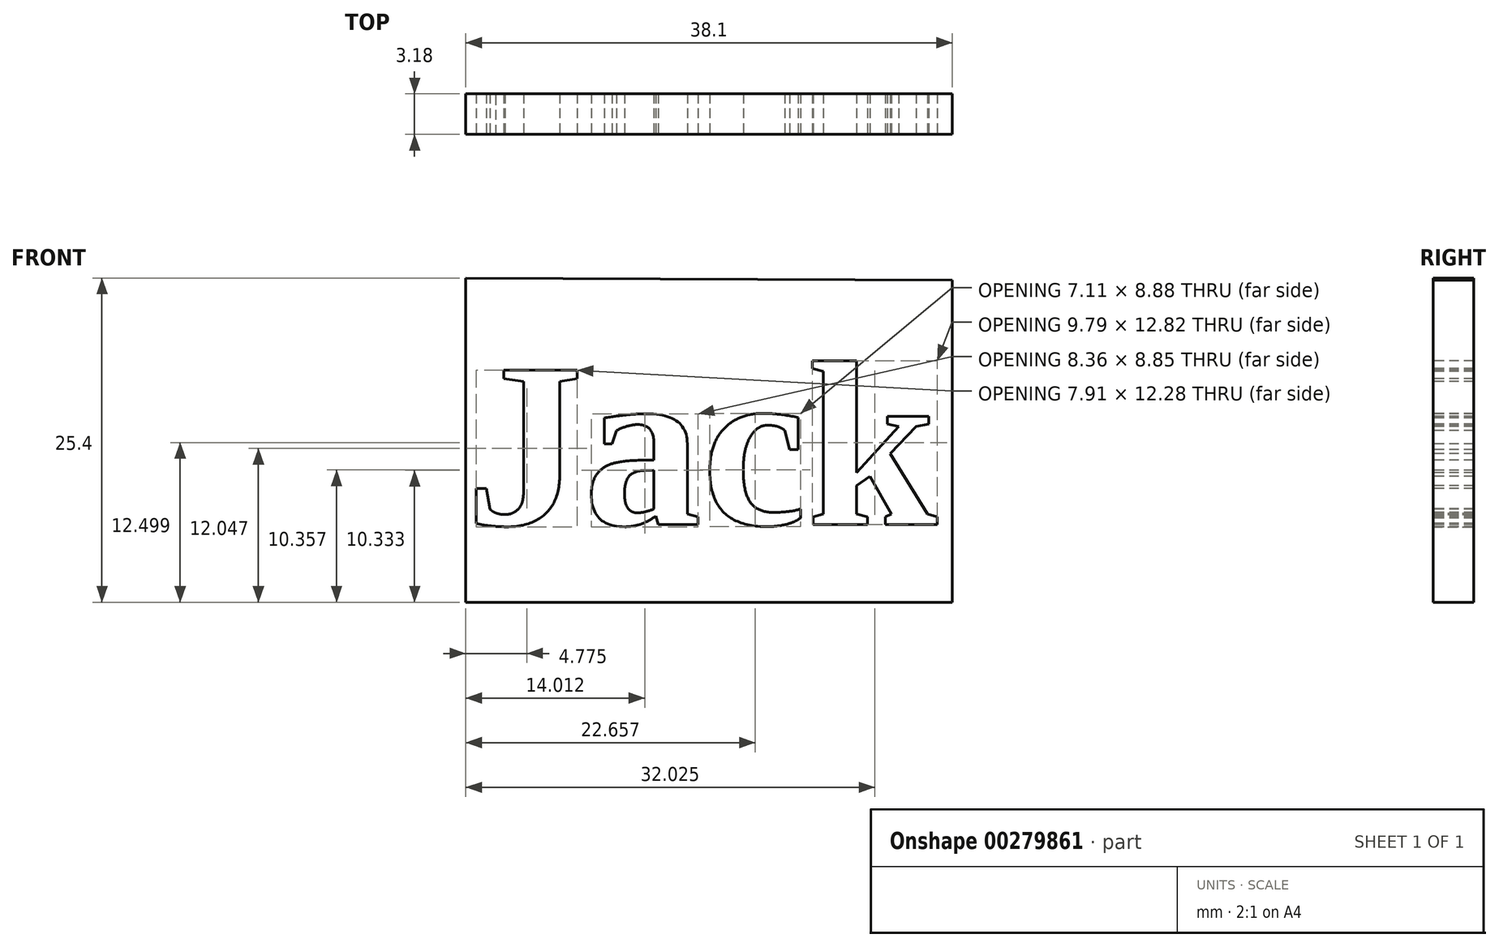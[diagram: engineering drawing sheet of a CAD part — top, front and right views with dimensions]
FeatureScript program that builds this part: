
annotation { "Feature Type Name" : "Feature", "Feature Type Description" : "" }
export const myFeature = defineFeature(function(context is Context, id is Id, definition is map)
    precondition{}
    {
        {
            var Q0;
            Q0=qCreatedBy(makeId("Front.planeOp"),FACE);
            var sketch = newSketch(context, id + "F0", { "sketchPlane" : qUnion([Q0])});
            skLineSegment(sketch, "E0", {"start": v(-38.1, 25.4) * mm, "end": v(-38.1, 0) * mm});
            skLineSegment(sketch, "E1", {"start": v(-38.1, 0) * mm, "end": v(0, 0) * mm});
            skLineSegment(sketch, "E2", {"start": v(0, 0) * mm, "end": v(0, 25.24) * mm});
            skLineSegment(sketch, "E3", {"start": v(0, 25.24) * mm, "end": v(-38.1, 25.4) * mm});
            skSolve(sketch);
        }
        {
            var Q0;
            Q0=makeQuery(id+"F0.imprint","IMPRINT",FACE,{"disambiguationData":[TD([[makeQuery(id+"F0.imprint","IMPRINT",EDGE,{"derivedFrom":sQuery(id+"F0.wireOp",EDGE,"E0")}),1.0]])]});
            extrude(context, id + "F1", {"entities" : qUnion([Q0]), "depth" : 3.17 * mm});
        }
        {
            var Q0;
            Q0=makeQuery(id+"F1.opExtrude","CAP_FACE",FACE,{"disambiguationData":[OSD([sQuery(id+"F0.wireOp",EDGE,"E0"),sQuery(id+"F0.wireOp",EDGE,"E1"),sQuery(id+"F0.wireOp",EDGE,"E2"),sQuery(id+"F0.wireOp",EDGE,"E3")])],"isStart":false});
            var sketch = newSketch(context, id + "F2", { "sketchPlane" : qUnion([Q0])});
            skText(sketch, "E4", { "text": "Jack", "fontName": "Tinos-Bold.ttf"});
            const initialGuessF2  = {"E4": [-0.0381, 0.00609, 1, 0, 0.0133]};
            skSetInitialGuess(sketch, initialGuessF2);
            skSolve(sketch);
        }
        {
            var Q0;
            Q0=makeQuery(id+"F2.imprint","IMPRINT",FACE,{"disambiguationData":[TD([[makeQuery(id+"F2.imprint","IMPRINT",EDGE,{"derivedFrom":sQuery(id+"F2.wireOp",EDGE,"E4.sketch_text.stroke-0")}),-1.0]])]});
            var Q1;
            Q1=makeQuery(id+"F2.imprint","IMPRINT",FACE,{"disambiguationData":[TD([[makeQuery(id+"F2.imprint","IMPRINT",EDGE,{"derivedFrom":sQuery(id+"F2.wireOp",EDGE,"E4.sketch_text.stroke-18")}),-1.0]])]});
            var Q2;
            Q2=makeQuery(id+"F2.imprint","IMPRINT",FACE,{"disambiguationData":[TD([[makeQuery(id+"F2.imprint","IMPRINT",EDGE,{"derivedFrom":sQuery(id+"F2.wireOp",EDGE,"E4.sketch_text.stroke-46")}),-1.0]])]});
            var Q3;
            Q3=makeQuery(id+"F2.imprint","IMPRINT",FACE,{"disambiguationData":[TD([[makeQuery(id+"F2.imprint","IMPRINT",EDGE,{"derivedFrom":sQuery(id+"F2.wireOp",EDGE,"E4.sketch_text.stroke-66")}),-1.0]])]});
            extrude(context, id + "F3", {"entities" : qUnion([Q0, Q1, Q2, Q3]), "operationType" : NewBodyOperationType.REMOVE, "oppositeDirection" : true, "depth" : 3.17 * mm});
        }
    });
